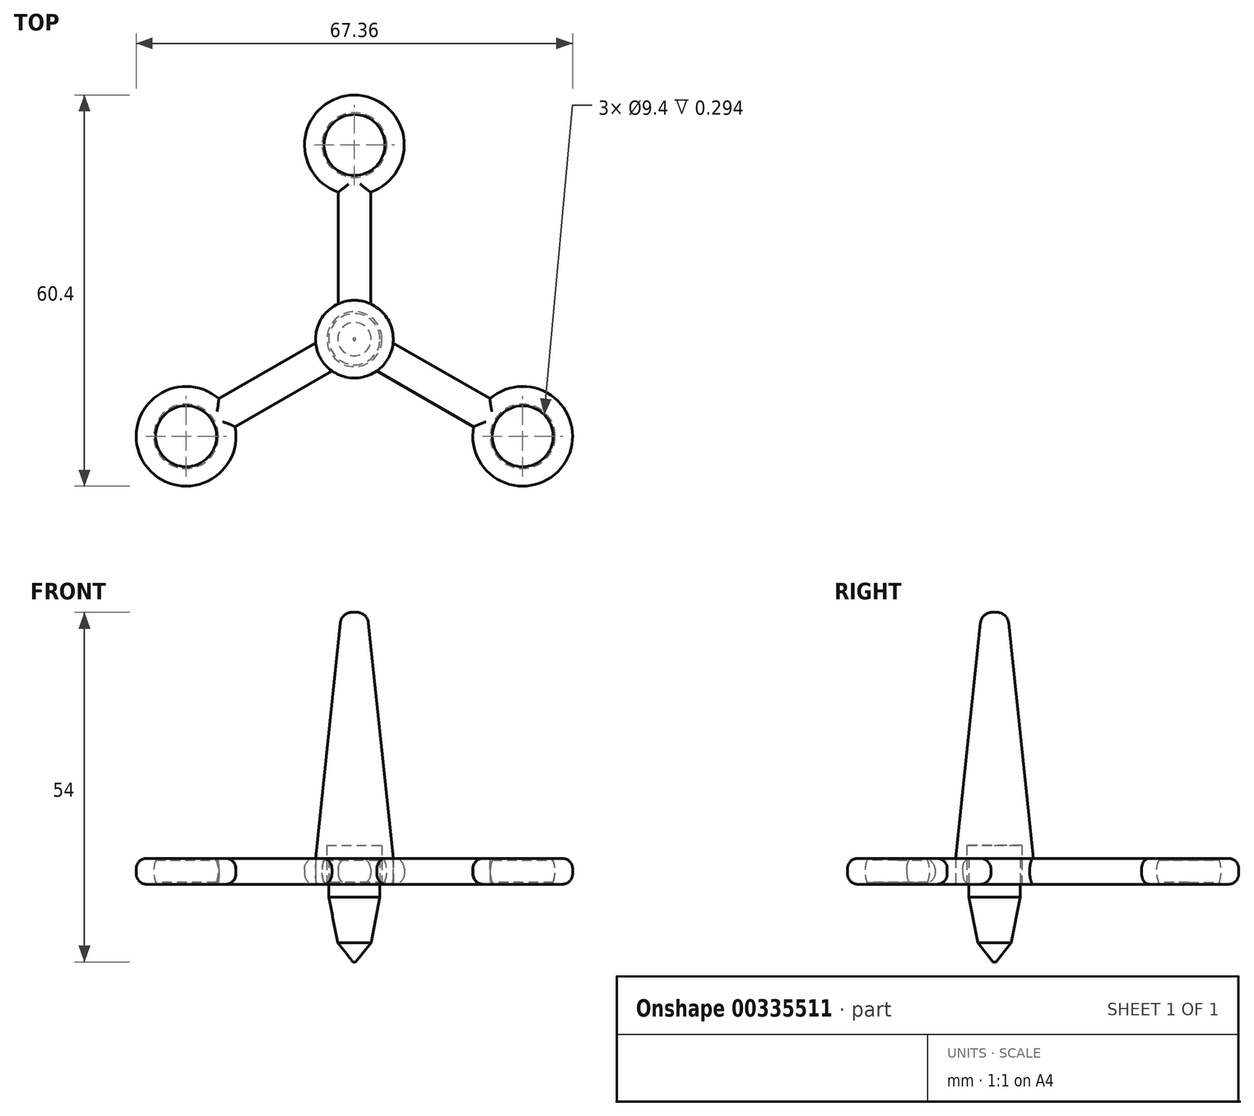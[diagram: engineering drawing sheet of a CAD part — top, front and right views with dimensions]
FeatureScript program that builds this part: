
annotation { "Feature Type Name" : "Feature", "Feature Type Description" : "" }
export const myFeature = defineFeature(function(context is Context, id is Id, definition is map)
    precondition{}
    {
        {
            var Q0;
            Q0=qCreatedBy(makeId("Top.planeOp"),FACE);
            var sketch = newSketch(context, id + "F0", { "sketchPlane" : qUnion([Q0])});
            skCircle(sketch, "E0", {"center": v(0, 0) * mm, "radius": 6 * mm});
            skCircle(sketch, "E1", {"center": v(0, 30) * mm, "radius": 4.7 * mm});
            skCircle(sketch, "E2.0", {"center": v(0, 30) * mm, "radius": 7.7 * mm});
            skLineSegment(sketch, "E3", {"start": v(-2.5, 22.72) * mm, "end": v(-2.5, 5.45) * mm});
            skLineSegment(sketch, "E4", {"start": v(2.5, 5.45) * mm, "end": v(2.5, 22.72) * mm});
            skCircle(sketch, "E5.1.0", {"center": v(-25.98, -15) * mm, "radius": 4.7 * mm});
            skCircle(sketch, "E5.1.1", {"center": v(-25.98, -15) * mm, "radius": 7.7 * mm});
            skLineSegment(sketch, "E5.1.2", {"start": v(-18.42, -13.52) * mm, "end": v(-3.47, -4.9) * mm});
            skLineSegment(sketch, "E5.1.3", {"start": v(-5.97, -0.56) * mm, "end": v(-20.92, -9.2) * mm});
            skCircle(sketch, "E5.2.0", {"center": v(25.98, -15) * mm, "radius": 4.7 * mm});
            skCircle(sketch, "E5.2.1", {"center": v(25.98, -15) * mm, "radius": 7.7 * mm});
            skLineSegment(sketch, "E5.2.2", {"start": v(20.92, -9.2) * mm, "end": v(5.97, -0.56) * mm});
            skLineSegment(sketch, "E5.2.3", {"start": v(3.47, -4.9) * mm, "end": v(18.42, -13.52) * mm});
            skSolve(sketch);
        }
        {
            var Q0;
            {var subQ0=sQuery(id+"F0.wireOp",EDGE,"E0");var subQ4=makeQuery(id+"F0.imprint","INTERSECT",VERTEX,{"derivedFrom":[subQ0,sQuery(id+"F0.wireOp",EDGE,"E3")]});Q0=makeQuery(id+"F0.imprint","IMPRINT",FACE,{"disambiguationData":[TD([[makeQuery(id+"F0.imprint","IMPRINT",EDGE,{"disambiguationData":[TD([[subQ4,1.0]])],"derivedFrom":subQ0}),1.0]])]});}
            extrude(context, id + "F1", {"entities" : qUnion([Q0]), "depth" : 2 * mm, "hasSecondDirection" : true, "secondDirectionOppositeDirection" : true, "secondDirectionDepth" : 2 * mm});
        }
        {
            var Q0;
            Q0=qCreatedBy(makeId("Top.planeOp"),FACE);
            cPlane(context, id + "F2", {"entities" : qUnion([Q0]), "cplaneType" : CPlaneType.OFFSET, "offset" : 40 * mm, "width" : 150 * mm, "height" : 150 * mm});
        }
        {
            var Q0;
            Q0=qCreatedBy(id+"F2.planeOp",FACE);
            var sketch = newSketch(context, id + "F3", { "sketchPlane" : qUnion([Q0])});
            skCircle(sketch, "E6", {"center": v(0, 0) * mm, "radius": 2 * mm});
            skSolve(sketch);
        }
        {
            var Q1;
            Q1=makeQuery(id+"F3.imprint","IMPRINT",FACE,{"disambiguationData":[TD([[makeQuery(id+"F3.imprint","IMPRINT",EDGE,{"derivedFrom":sQuery(id+"F3.wireOp",EDGE,"E6")}),1.0]])]});
            var Q2;
            Q2=makeQuery(id+"F1.opExtrude","CAP_FACE",FACE,{"disambiguationData":[OSD([sQuery(id+"F0.wireOp",EDGE,"E0")])],"isStart":false});
            loft(context, id + "F4", {"operationType" : NewBodyOperationType.ADD, "sheetProfilesArray" : [{ "sheetProfileEntities" : qUnion([Q1]) }, { "sheetProfileEntities" : qUnion([Q2]) }]});
        }
        {
            var Q0;
            {var subQ0=sQuery(id+"F0.wireOp",EDGE,"E5.1.2");Q0=makeQuery(id+"F0.imprint","IMPRINT",FACE,{"disambiguationData":[TD([[makeQuery(id+"F0.imprint","IMPRINT",EDGE,{"derivedFrom":subQ0}),1.0]])]});}
            var Q1;
            Q1=makeQuery(id+"F0.imprint","IMPRINT",FACE,{"disambiguationData":[TD([[makeQuery(id+"F0.imprint","IMPRINT",EDGE,{"derivedFrom":sQuery(id+"F0.wireOp",EDGE,"E5.1.0")}),-1.0]])]});
            var Q2;
            {var subQ0=sQuery(id+"F0.wireOp",EDGE,"E5.2.2");Q2=makeQuery(id+"F0.imprint","IMPRINT",FACE,{"disambiguationData":[TD([[makeQuery(id+"F0.imprint","IMPRINT",EDGE,{"derivedFrom":subQ0}),1.0]])]});}
            var Q3;
            Q3=makeQuery(id+"F0.imprint","IMPRINT",FACE,{"disambiguationData":[TD([[makeQuery(id+"F0.imprint","IMPRINT",EDGE,{"derivedFrom":sQuery(id+"F0.wireOp",EDGE,"E5.2.0")}),-1.0]])]});
            var Q4;
            {var subQ0=sQuery(id+"F0.wireOp",EDGE,"E3");Q4=makeQuery(id+"F0.imprint","IMPRINT",FACE,{"disambiguationData":[TD([[makeQuery(id+"F0.imprint","IMPRINT",EDGE,{"derivedFrom":subQ0}),1.0]])]});}
            var Q5;
            Q5=makeQuery(id+"F0.imprint","IMPRINT",FACE,{"disambiguationData":[TD([[makeQuery(id+"F0.imprint","IMPRINT",EDGE,{"derivedFrom":sQuery(id+"F0.wireOp",EDGE,"E1")}),-1.0]])]});
            extrude(context, id + "F5", {"entities" : qUnion([Q0, Q1, Q2, Q3, Q4, Q5]), "operationType" : NewBodyOperationType.ADD, "depth" : 2 * mm, "hasSecondDirection" : true, "secondDirectionOppositeDirection" : true, "secondDirectionDepth" : 2 * mm});
        }
        {
            var Q0;
            {var subQ0=sQuery(id+"F0.wireOp",EDGE,"E0");Q0=makeQuery(id+"F5.boolean.opBoolean","MERGE",FACE,{"derivedFrom":[makeQuery(id+"F1.opExtrude","CAP_FACE",FACE,{"disambiguationData":[OSD([subQ0])],"isStart":true}),makeQuery(id+"F5.opExtrude","CAP_FACE",FACE,{"disambiguationData":[OSD([subQ0,sQuery(id+"F0.wireOp",EDGE,"E1"),sQuery(id+"F0.wireOp",EDGE,"E2.0"),sQuery(id+"F0.wireOp",EDGE,"E3"),sQuery(id+"F0.wireOp",EDGE,"E4")])],"isStart":true}),makeQuery(id+"F5.opExtrude","CAP_FACE",FACE,{"disambiguationData":[OSD([subQ0,sQuery(id+"F0.wireOp",EDGE,"E5.1.0"),sQuery(id+"F0.wireOp",EDGE,"E5.1.1"),sQuery(id+"F0.wireOp",EDGE,"E5.1.2"),sQuery(id+"F0.wireOp",EDGE,"E5.1.3")])],"isStart":true}),makeQuery(id+"F5.opExtrude","CAP_FACE",FACE,{"disambiguationData":[OSD([subQ0,sQuery(id+"F0.wireOp",EDGE,"E5.2.0"),sQuery(id+"F0.wireOp",EDGE,"E5.2.1"),sQuery(id+"F0.wireOp",EDGE,"E5.2.2"),sQuery(id+"F0.wireOp",EDGE,"E5.2.3")])],"isStart":true})]});}
            var sketch = newSketch(context, id + "F6", { "sketchPlane" : qUnion([Q0])});
            skCircle(sketch, "E7", {"center": v(0, 0) * mm, "radius": 4.25 * mm});
            skSolve(sketch);
        }
        {
            var Q0;
            Q0=makeQuery(id+"F6.imprint","IMPRINT",FACE,{"disambiguationData":[TD([[makeQuery(id+"F6.imprint","IMPRINT",EDGE,{"derivedFrom":sQuery(id+"F6.wireOp",EDGE,"E7")}),1.0]])]});
            extrude(context, id + "F7", {"entities" : qUnion([Q0]), "operationType" : NewBodyOperationType.REMOVE, "oppositeDirection" : true, "depth" : 6 * mm});
        }
        {
            var Q0;
            Q0=makeQuery(id+"F4.opLoft","MID_CAP_EDGE",EDGE,{"disambiguationData":[OSD([sQuery(id+"F3.wireOp",EDGE,"E6")])],"capPos":0.0});
            fillet(context, id + "F8", {"entities" : qUnion([Q0]), "radius" : 1.8 * mm, "tangentPropagation" : true, "allowEdgeOverflow" : false});
        }
        {
            var Q0;
            Q0=makeQuery(id+"F5.opExtrude","CAP_EDGE",EDGE,{"disambiguationData":[OSD([sQuery(id+"F0.wireOp",EDGE,"E5.2.3")])],"isStart":false});
            var Q1;
            Q1=makeQuery(id+"F5.opExtrude","CAP_EDGE",EDGE,{"disambiguationData":[OSD([sQuery(id+"F0.wireOp",EDGE,"E5.2.1")])],"isStart":false});
            var Q2;
            Q2=makeQuery(id+"F5.opExtrude","CAP_EDGE",EDGE,{"disambiguationData":[OSD([sQuery(id+"F0.wireOp",EDGE,"E5.2.2")])],"isStart":false});
            var Q3;
            Q3=makeQuery(id+"F5.opExtrude","CAP_EDGE",EDGE,{"disambiguationData":[OSD([sQuery(id+"F0.wireOp",EDGE,"E5.1.2")])],"isStart":false});
            var Q4;
            Q4=makeQuery(id+"F5.opExtrude","CAP_EDGE",EDGE,{"disambiguationData":[OSD([sQuery(id+"F0.wireOp",EDGE,"E5.1.3")])],"isStart":false});
            var Q5;
            Q5=makeQuery(id+"F5.opExtrude","CAP_EDGE",EDGE,{"disambiguationData":[OSD([sQuery(id+"F0.wireOp",EDGE,"E5.1.1")])],"isStart":false});
            var Q6;
            Q6=makeQuery(id+"F5.opExtrude","CAP_EDGE",EDGE,{"disambiguationData":[OSD([sQuery(id+"F0.wireOp",EDGE,"E3")])],"isStart":false});
            var Q7;
            Q7=makeQuery(id+"F5.opExtrude","CAP_EDGE",EDGE,{"disambiguationData":[OSD([sQuery(id+"F0.wireOp",EDGE,"E4")])],"isStart":false});
            var Q8;
            Q8=makeQuery(id+"F5.opExtrude","CAP_EDGE",EDGE,{"disambiguationData":[OSD([sQuery(id+"F0.wireOp",EDGE,"E2.0")])],"isStart":false});
            var Q9;
            Q9=makeQuery(id+"F5.opExtrude","CAP_EDGE",EDGE,{"disambiguationData":[OSD([sQuery(id+"F0.wireOp",EDGE,"E5.2.1")])],"isStart":true});
            var Q10;
            Q10=makeQuery(id+"F5.opExtrude","CAP_EDGE",EDGE,{"disambiguationData":[OSD([sQuery(id+"F0.wireOp",EDGE,"E5.2.3")])],"isStart":true});
            var Q11;
            Q11=makeQuery(id+"F5.opExtrude","CAP_EDGE",EDGE,{"disambiguationData":[OSD([sQuery(id+"F0.wireOp",EDGE,"E5.2.2")])],"isStart":true});
            var Q12;
            Q12=makeQuery(id+"F5.opExtrude","CAP_EDGE",EDGE,{"disambiguationData":[OSD([sQuery(id+"F0.wireOp",EDGE,"E4")])],"isStart":true});
            var Q13;
            Q13=makeQuery(id+"F5.opExtrude","CAP_EDGE",EDGE,{"disambiguationData":[OSD([sQuery(id+"F0.wireOp",EDGE,"E3")])],"isStart":true});
            var Q14;
            Q14=makeQuery(id+"F5.opExtrude","CAP_EDGE",EDGE,{"disambiguationData":[OSD([sQuery(id+"F0.wireOp",EDGE,"E5.1.3")])],"isStart":true});
            var Q15;
            Q15=makeQuery(id+"F5.opExtrude","CAP_EDGE",EDGE,{"disambiguationData":[OSD([sQuery(id+"F0.wireOp",EDGE,"E5.1.2")])],"isStart":true});
            var Q16;
            Q16=makeQuery(id+"F5.opExtrude","CAP_EDGE",EDGE,{"disambiguationData":[OSD([sQuery(id+"F0.wireOp",EDGE,"E5.1.1")])],"isStart":true});
            var Q17;
            Q17=makeQuery(id+"F5.opExtrude","CAP_EDGE",EDGE,{"disambiguationData":[OSD([sQuery(id+"F0.wireOp",EDGE,"E2.0")])],"isStart":true});
            fillet(context, id + "F9", {"entities" : qUnion([Q0, Q1, Q2, Q3, Q4, Q5, Q6, Q7, Q8, Q9, Q10, Q11, Q12, Q13, Q14, Q15, Q16, Q17]), "radius" : 1.6 * mm, "tangentPropagation" : true, "allowEdgeOverflow" : false});
        }
        {
            var Q0;
            Q0=qCreatedBy(makeId("Right.planeOp"),FACE);
            var sketch = newSketch(context, id + "F10", { "sketchPlane" : qUnion([Q0])});
            skPoint(sketch, "E8.0", {"position": v(30, 0) * mm});
            skLineSegment(sketch, "E9", {"start": v(30, 10.68) * mm, "end": v(30, -11.66) * mm, "construction": true});
            skArc(sketch, "E10", {"start": v(30, 5) * mm, "mid": v(25, 0) * mm, "end": v(30, -5) * mm});
            skLineSegment(sketch, "E11", {"start": v(30, 5) * mm, "end": v(30, -5) * mm});
            skSolve(sketch);
        }
        {
            var Q0;
            Q0=makeQuery(id+"F10.imprint","IMPRINT",FACE,{"disambiguationData":[TD([[makeQuery(id+"F10.imprint","IMPRINT",EDGE,{"derivedFrom":sQuery(id+"F10.wireOp",EDGE,"E10")}),1.0]])]});
            var Q1;
            Q1=sQuery(id+"F10.wireOp",EDGE,"E9");
            revolve(context, id + "F11", {"entities" : qUnion([Q0]), "axis" : qUnion([Q1]), "revolveType" : RevolveType.FULL});
        }
        {
            var Q0;
            Q0=qCreatedBy(makeId("Front.planeOp"),FACE);
            var Q1;
            Q1=sQuery(id+"F0.wireOp",VERTEX,"E5.1.0.center");
            cPlane(context, id + "F12", {"entities" : qUnion([Q0, Q1]), "cplaneType" : CPlaneType.PLANE_POINT, "offset" : 25 * mm, "width" : 150 * mm, "height" : 150 * mm});
        }
        {
            var Q0;
            Q0=qCreatedBy(id+"F12.planeOp",FACE);
            var sketch = newSketch(context, id + "F13", { "sketchPlane" : qUnion([Q0])});
            skPoint(sketch, "E12.0", {"position": v(-25.98, 0) * mm});
            skPoint(sketch, "E12.1", {"position": v(25.98, 0) * mm});
            skLineSegment(sketch, "E13", {"start": v(-25.98, 15.38) * mm, "end": v(-25.98, -14.43) * mm, "construction": true});
            skLineSegment(sketch, "E14", {"start": v(25.98, 16.6) * mm, "end": v(25.98, -18.9) * mm, "construction": true});
            skArc(sketch, "E15", {"start": v(-25.98, -5) * mm, "mid": v(-20.98, 0) * mm, "end": v(-25.98, 5) * mm});
            skArc(sketch, "E16", {"start": v(25.98, -5) * mm, "mid": v(30.98, 0) * mm, "end": v(25.98, 5) * mm});
            skLineSegment(sketch, "E17", {"start": v(-25.98, 5) * mm, "end": v(-25.98, -5) * mm});
            skLineSegment(sketch, "E18", {"start": v(25.98, 5) * mm, "end": v(25.98, -5) * mm});
            skSolve(sketch);
        }
        {
            var Q0;
            Q0=makeQuery(id+"F13.imprint","IMPRINT",FACE,{"disambiguationData":[TD([[makeQuery(id+"F13.imprint","IMPRINT",EDGE,{"derivedFrom":sQuery(id+"F13.wireOp",EDGE,"E15")}),1.0]])]});
            var Q1;
            Q1=sQuery(id+"F13.wireOp",EDGE,"E13");
            revolve(context, id + "F14", {"entities" : qUnion([Q0]), "axis" : qUnion([Q1]), "revolveType" : RevolveType.FULL});
        }
        {
            var Q0;
            Q0=makeQuery(id+"F13.imprint","IMPRINT",FACE,{"disambiguationData":[TD([[makeQuery(id+"F13.imprint","IMPRINT",EDGE,{"derivedFrom":sQuery(id+"F13.wireOp",EDGE,"E16")}),1.0]])]});
            var Q1;
            Q1=sQuery(id+"F13.wireOp",EDGE,"E14");
            revolve(context, id + "F15", {"entities" : qUnion([Q0]), "axis" : qUnion([Q1]), "revolveType" : RevolveType.FULL});
        }
        {
            var Q0;
            {var subQ0=sQuery(id+"F0.wireOp",EDGE,"E0");Q0=makeQuery(id+"F5.boolean.opBoolean","MERGE",FACE,{"derivedFrom":[makeQuery(id+"F1.opExtrude","CAP_FACE",FACE,{"disambiguationData":[OSD([subQ0])],"isStart":true}),makeQuery(id+"F5.opExtrude","CAP_FACE",FACE,{"disambiguationData":[OSD([subQ0,sQuery(id+"F0.wireOp",EDGE,"E1"),sQuery(id+"F0.wireOp",EDGE,"E2.0"),sQuery(id+"F0.wireOp",EDGE,"E3"),sQuery(id+"F0.wireOp",EDGE,"E4")])],"isStart":true}),makeQuery(id+"F5.opExtrude","CAP_FACE",FACE,{"disambiguationData":[OSD([subQ0,sQuery(id+"F0.wireOp",EDGE,"E5.1.0"),sQuery(id+"F0.wireOp",EDGE,"E5.1.1"),sQuery(id+"F0.wireOp",EDGE,"E5.1.2"),sQuery(id+"F0.wireOp",EDGE,"E5.1.3")])],"isStart":true}),makeQuery(id+"F5.opExtrude","CAP_FACE",FACE,{"disambiguationData":[OSD([subQ0,sQuery(id+"F0.wireOp",EDGE,"E5.2.0"),sQuery(id+"F0.wireOp",EDGE,"E5.2.1"),sQuery(id+"F0.wireOp",EDGE,"E5.2.2"),sQuery(id+"F0.wireOp",EDGE,"E5.2.3")])],"isStart":true})]});}
            var sketch = newSketch(context, id + "F16", { "sketchPlane" : qUnion([Q0])});
            skCircle(sketch, "E19", {"center": v(0, 0) * mm, "radius": 3.95 * mm});
            skSolve(sketch);
        }
        {
            var Q0;
            Q0=makeQuery(id+"F16.imprint","IMPRINT",FACE,{"disambiguationData":[TD([[makeQuery(id+"F16.imprint","IMPRINT",EDGE,{"derivedFrom":sQuery(id+"F16.wireOp",EDGE,"E19")}),1.0]])]});
            extrude(context, id + "F17", {"entities" : qUnion([Q0]), "oppositeDirection" : true, "depth" : 4 * mm, "hasSecondDirection" : true, "secondDirectionOppositeDirection" : false, "secondDirectionDepth" : 2 * mm});
        }
        {
            var Q0;
            Q0=makeQuery(id+"F17.opExtrude","CAP_FACE",FACE,{"disambiguationData":[OSD([sQuery(id+"F16.wireOp",EDGE,"E19")])],"isStart":true});
            cPlane(context, id + "F18", {"entities" : qUnion([Q0]), "cplaneType" : CPlaneType.OFFSET, "offset" : 10 * mm, "width" : 150 * mm, "height" : 150 * mm});
        }
        {
            var Q0;
            Q0=qCreatedBy(id+"F18.planeOp",FACE);
            var sketch = newSketch(context, id + "F19", { "sketchPlane" : qUnion([Q0])});
            skCircle(sketch, "E20", {"center": v(0, 0) * mm, "radius": 2 * mm});
            skSolve(sketch);
        }
        {
            var Q1;
            Q1=makeQuery(id+"F17.opExtrude","CAP_FACE",FACE,{"disambiguationData":[OSD([sQuery(id+"F16.wireOp",EDGE,"E19")])],"isStart":true});
            var Q2;
            Q2=makeQuery(id+"F19.imprint","IMPRINT",FACE,{"disambiguationData":[TD([[makeQuery(id+"F19.imprint","IMPRINT",EDGE,{"derivedFrom":sQuery(id+"F19.wireOp",EDGE,"E20")}),1.0]])]});
            loft(context, id + "F20", {"operationType" : NewBodyOperationType.ADD, "sheetProfilesArray" : [{ "sheetProfileEntities" : qUnion([Q1]) }, { "sheetProfileEntities" : qUnion([Q2]) }]});
        }
        {
            var Q0;
            Q0=makeQuery(id+"F20.opLoft","MID_CAP_EDGE",EDGE,{"disambiguationData":[OSD([sQuery(id+"F16.wireOp",EDGE,"E19"),sQuery(id+"F19.wireOp",EDGE,"E20")])],"capPos":1.0});
            chamfer(context, id + "F21", {"entities" : qUnion([Q0]), "chamferType" : ChamferType.TWO_OFFSETS, "width1" : 1.8 * mm, "oppositeDirection" : false, "width2" : 3 * mm, "tangentPropagation" : true});
        }
        {
            var Q0;
            Q0=makeQuery(id+"F15.opRevolve","SWEPT_BODY",BODY,{"disambiguationData":[OSD([sQuery(id+"F13.wireOp",EDGE,"E16"),sQuery(id+"F13.wireOp",EDGE,"E18")])]});
            var Q1;
            Q1=makeQuery(id+"F14.opRevolve","SWEPT_BODY",BODY,{"disambiguationData":[OSD([sQuery(id+"F13.wireOp",EDGE,"E15"),sQuery(id+"F13.wireOp",EDGE,"E17")])]});
            var Q2;
            Q2=makeQuery(id+"F11.opRevolve","SWEPT_BODY",BODY,{"disambiguationData":[OSD([sQuery(id+"F10.wireOp",EDGE,"E10"),sQuery(id+"F10.wireOp",EDGE,"E11")])]});
            var Q3;
            Q3=makeQuery(id+"F1.opExtrude","SWEPT_BODY",BODY,{"disambiguationData":[OSD([sQuery(id+"F0.wireOp",EDGE,"E0")])]});
            booleanBodies(context, id + "F22", {"operationType" : BooleanOperationType.SUBTRACTION, "tools" : qUnion([Q0, Q1, Q2]), "targets" : qUnion([Q3])});
        }
    });
